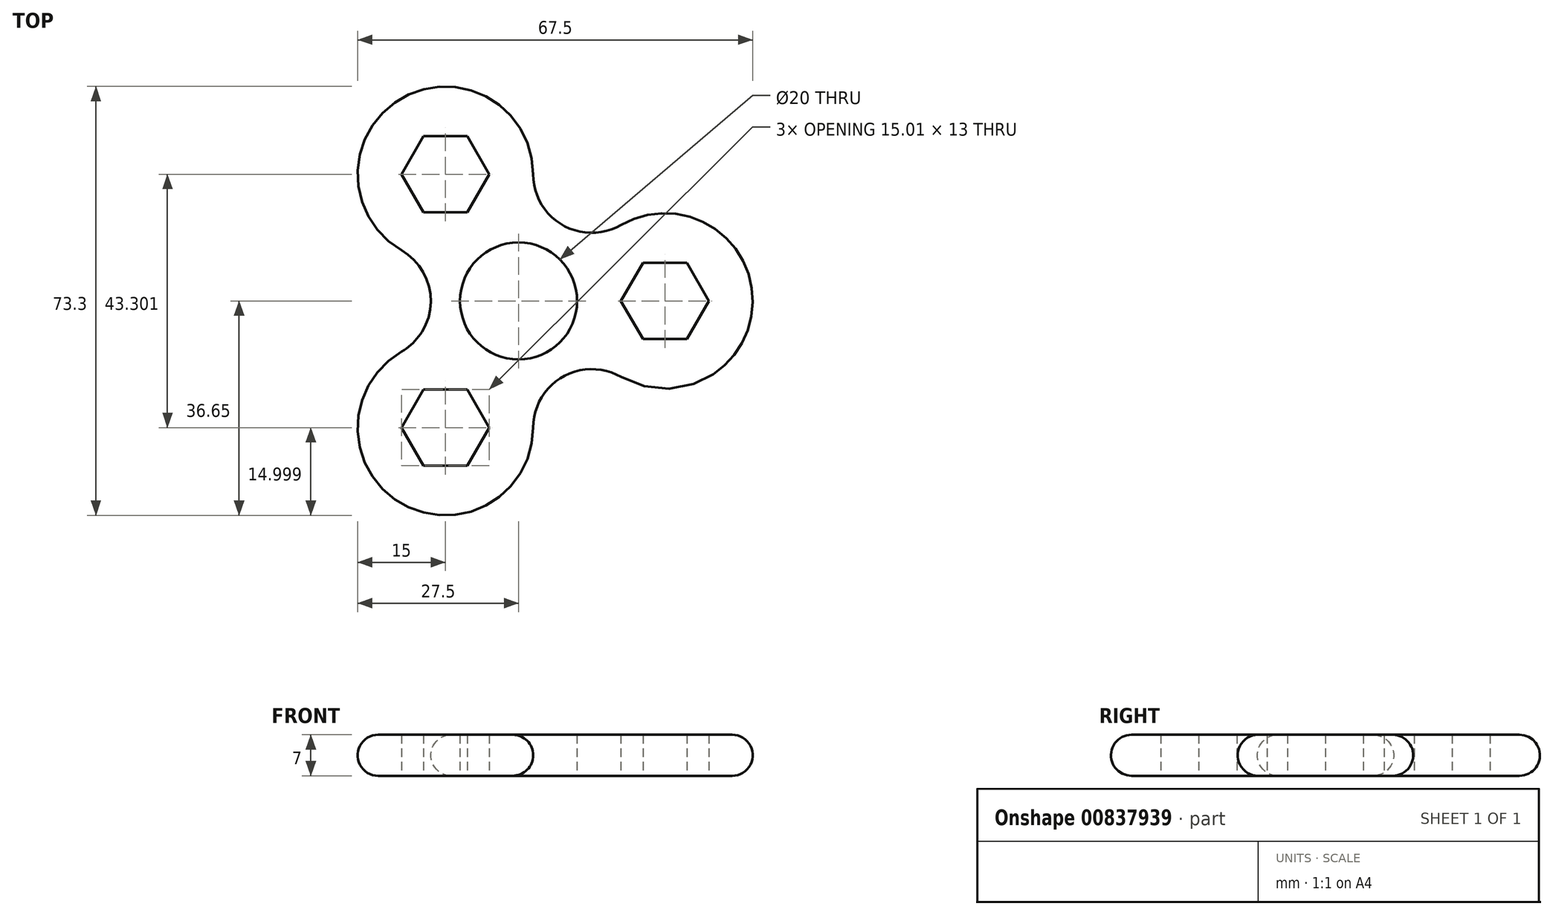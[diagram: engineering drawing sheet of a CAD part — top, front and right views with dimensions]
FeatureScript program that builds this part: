
annotation { "Feature Type Name" : "Feature", "Feature Type Description" : "" }
export const myFeature = defineFeature(function(context is Context, id is Id, definition is map)
    precondition{}
    {
        {
            var Q0;
            Q0=qCreatedBy(makeId("Top.planeOp"),FACE);
            var sketch = newSketch(context, id + "F0", { "sketchPlane" : qUnion([Q0])});
            skLineSegment(sketch, "E0", {"start": v(0, 0) * mm, "end": v(25, 0) * mm, "construction": true});
            skArc(sketch, "E1", {"start": v(17.5, -13) * mm, "mid": v(40, 0) * mm, "end": v(17.5, 13) * mm});
            skArc(sketch, "E2.1.1", {"start": v(2.5, 21.65) * mm, "mid": v(-20, 34.64) * mm, "end": v(-20, 8.66) * mm});
            skLineSegment(sketch, "E2.1.2", {"start": v(0, 0) * mm, "end": v(-12.5, 21.65) * mm, "construction": true});
            skArc(sketch, "E2.2.1", {"start": v(-20, -8.66) * mm, "mid": v(-20, -34.64) * mm, "end": v(2.5, -21.65) * mm});
            skLineSegment(sketch, "E2.2.2", {"start": v(0, 0) * mm, "end": v(-12.5, -21.65) * mm, "construction": true});
            skPoint(sketch, "E2.center", {"position": v(0, 0) * mm});
            skArc(sketch, "E3", {"start": v(2.5, 21.65) * mm, "mid": v(7.5, 13) * mm, "end": v(17.5, 13) * mm});
            skArc(sketch, "E4.1.0", {"start": v(-20, -8.66) * mm, "mid": v(-15, 0) * mm, "end": v(-20, 8.66) * mm});
            skArc(sketch, "E4.2.0", {"start": v(17.5, -13) * mm, "mid": v(7.5, -13) * mm, "end": v(2.5, -21.65) * mm});
            skCircle(sketch, "E5", {"center": v(0, 0) * mm, "radius": 10 * mm});
            skCircle(sketch, "E6.cCircle", {"center": v(-12.5, -21.65) * mm, "radius": 6.5 * mm, "construction": true});
            skLineSegment(sketch, "E6.0", {"start": v(-8.75, -15.15) * mm, "end": v(-5, -21.65) * mm});
            skLineSegment(sketch, "E6.1", {"start": v(-5, -21.65) * mm, "end": v(-8.75, -28.15) * mm});
            skLineSegment(sketch, "E6.2", {"start": v(-8.75, -28.15) * mm, "end": v(-16.25, -28.15) * mm});
            skLineSegment(sketch, "E6.3", {"start": v(-16.25, -28.15) * mm, "end": v(-20, -21.65) * mm});
            skLineSegment(sketch, "E6.4", {"start": v(-20, -21.65) * mm, "end": v(-16.25, -15.15) * mm});
            skLineSegment(sketch, "E6.5", {"start": v(-16.25, -15.15) * mm, "end": v(-8.75, -15.15) * mm});
            skPoint(sketch, "E6.0.midPoint", {"position": v(-6.87, -18.4) * mm});
            skLineSegment(sketch, "E7.1.0", {"start": v(32.5, 0) * mm, "end": v(28.75, -6.5) * mm});
            skPoint(sketch, "E7.1.1", {"position": v(19.37, 3.25) * mm});
            skLineSegment(sketch, "E7.1.2", {"start": v(28.75, -6.5) * mm, "end": v(21.25, -6.5) * mm});
            skCircle(sketch, "E7.1.3", {"center": v(25, 0) * mm, "radius": 6.5 * mm, "construction": true});
            skLineSegment(sketch, "E7.1.4", {"start": v(28.75, 6.5) * mm, "end": v(32.5, 0) * mm});
            skLineSegment(sketch, "E7.1.5", {"start": v(21.25, -6.5) * mm, "end": v(17.5, 0) * mm});
            skLineSegment(sketch, "E7.1.6", {"start": v(17.5, 0) * mm, "end": v(21.25, 6.5) * mm});
            skLineSegment(sketch, "E7.1.7", {"start": v(21.25, 6.5) * mm, "end": v(28.75, 6.5) * mm});
            skLineSegment(sketch, "E7.2.0", {"start": v(-16.25, 28.15) * mm, "end": v(-8.75, 28.15) * mm});
            skPoint(sketch, "E7.2.1", {"position": v(-12.5, 15.15) * mm});
            skLineSegment(sketch, "E7.2.2", {"start": v(-8.75, 28.15) * mm, "end": v(-5, 21.65) * mm});
            skCircle(sketch, "E7.2.3", {"center": v(-12.5, 21.65) * mm, "radius": 6.5 * mm, "construction": true});
            skLineSegment(sketch, "E7.2.4", {"start": v(-20, 21.65) * mm, "end": v(-16.25, 28.15) * mm});
            skLineSegment(sketch, "E7.2.5", {"start": v(-5, 21.65) * mm, "end": v(-8.75, 15.15) * mm});
            skLineSegment(sketch, "E7.2.6", {"start": v(-8.75, 15.15) * mm, "end": v(-16.25, 15.15) * mm});
            skLineSegment(sketch, "E7.2.7", {"start": v(-16.25, 15.15) * mm, "end": v(-20, 21.65) * mm});
            skSolve(sketch);
        }
        {
            var Q0;
            Q0=qSketchRegion(id+"F0",true);
            extrude(context, id + "F1", {"entities" : qUnion([Q0]), "depth" : 7 * mm, "offsetDistance" : 25 * mm});
        }
        {
            var Q0;
            Q0=makeQuery(id+"F1.opExtrude","CAP_EDGE",EDGE,{"disambiguationData":[OSD([sQuery(id+"F0.wireOp",EDGE,"E2.1.1")])],"isStart":false});
            var Q1;
            Q1=makeQuery(id+"F1.opExtrude","CAP_EDGE",EDGE,{"disambiguationData":[OSD([sQuery(id+"F0.wireOp",EDGE,"E3")])],"isStart":true});
            fillet(context, id + "F2", {"entities" : qUnion([Q0, Q1]), "radius" : 3.5 * mm, "tangentPropagation" : true, "allowEdgeOverflow" : false});
        }
    });
